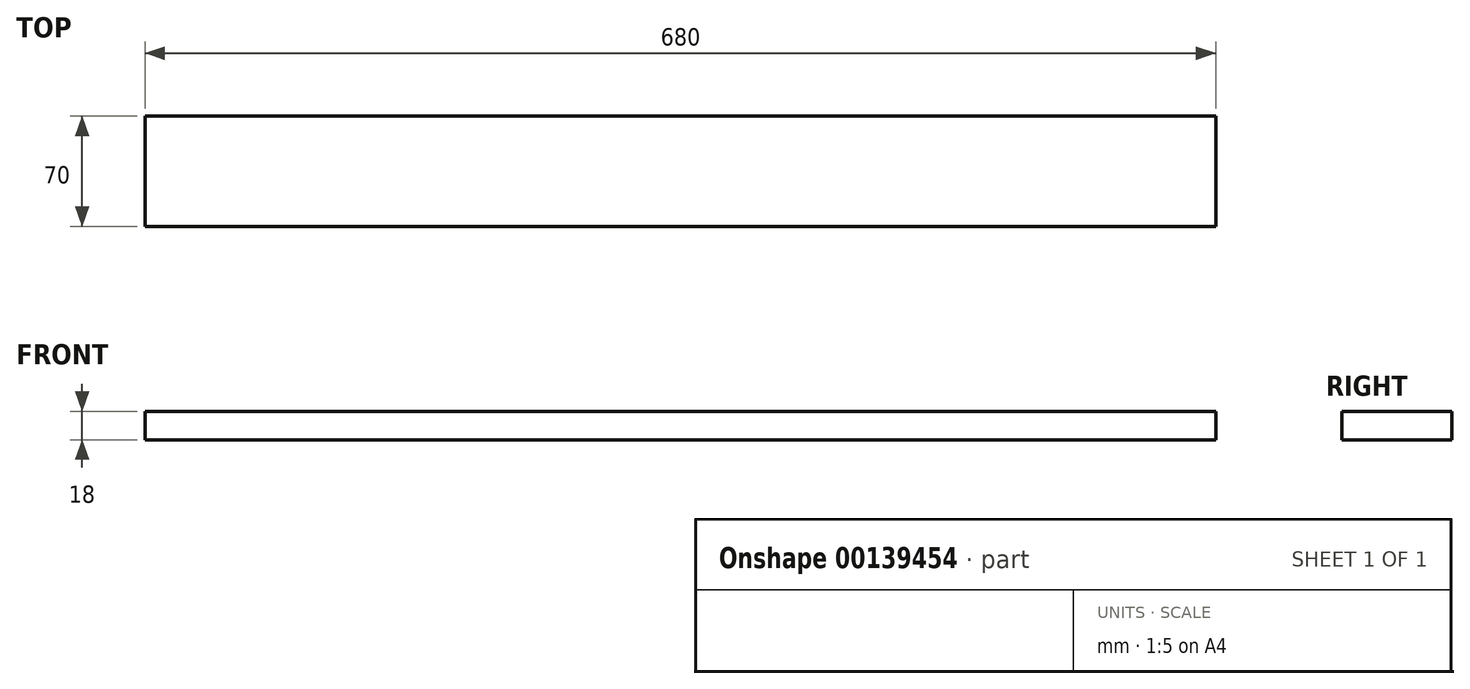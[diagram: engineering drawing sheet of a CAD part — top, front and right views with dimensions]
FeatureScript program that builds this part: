
annotation { "Feature Type Name" : "Feature", "Feature Type Description" : "" }
export const myFeature = defineFeature(function(context is Context, id is Id, definition is map)
    precondition{}
    {
        {
            var Q0;
            Q0=qCreatedBy(makeId("Top.planeOp"),FACE);
            var sketch = newSketch(context, id + "F0", { "sketchPlane" : qUnion([Q0])});
            skLineSegment(sketch, "E0.bottom", {"start": v(0, 0) * mm, "end": v(680, 0) * mm});
            skLineSegment(sketch, "E0.top", {"start": v(0, 70) * mm, "end": v(680, 70) * mm});
            skLineSegment(sketch, "E0.left", {"start": v(0, 0) * mm, "end": v(0, 70) * mm});
            skLineSegment(sketch, "E0.right", {"start": v(680, 0) * mm, "end": v(680, 70) * mm});
            skSolve(sketch);
        }
        {
            var Q0;
            Q0=makeQuery(id+"F0.imprint","IMPRINT",FACE,{"disambiguationData":[TD([[makeQuery(id+"F0.imprint","IMPRINT",EDGE,{"derivedFrom":sQuery(id+"F0.wireOp",EDGE,"E0.bottom")}),1.0]])]});
            extrude(context, id + "F1", {"entities" : qUnion([Q0]), "depth" : 18 * mm});
        }
    });
